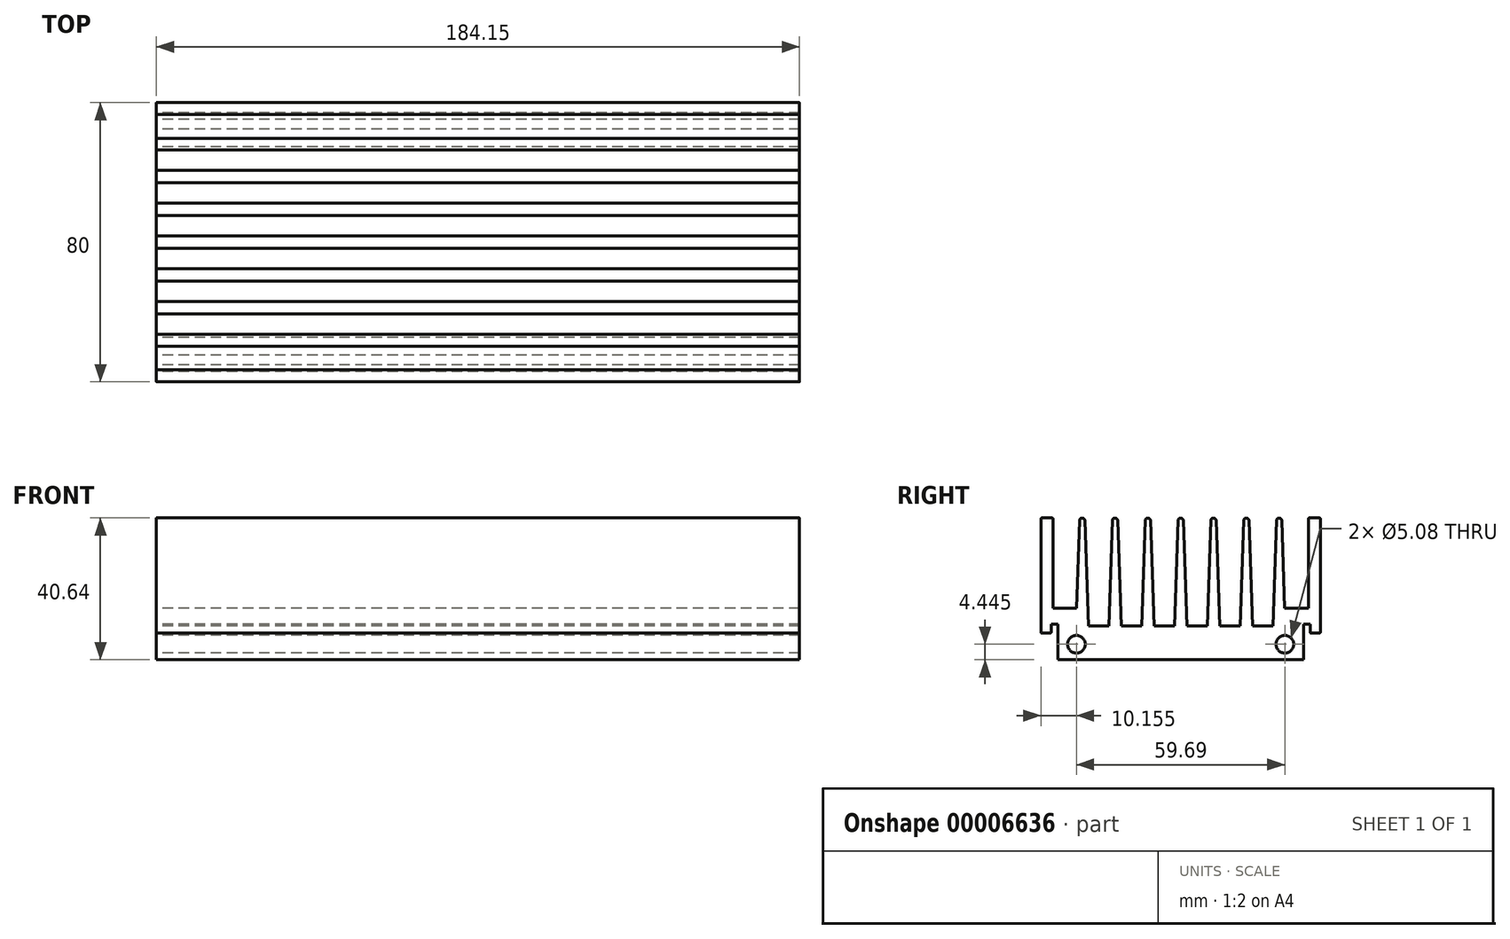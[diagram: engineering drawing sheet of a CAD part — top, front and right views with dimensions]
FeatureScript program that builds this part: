
annotation { "Feature Type Name" : "Feature", "Feature Type Description" : "" }
export const myFeature = defineFeature(function(context is Context, id is Id, definition is map)
    precondition{}
    {
        {
            var Q0;
            Q0=qCreatedBy(makeId("Right.planeOp"),FACE);
            var sketch = newSketch(context, id + "F0", { "sketchPlane" : qUnion([Q0])});
            skLineSegment(sketch, "E0", {"start": v(0, 0) * mm, "end": v(-35.18, 0) * mm});
            skLineSegment(sketch, "E1", {"start": v(-35.18, 0) * mm, "end": v(-35.18, 10.16) * mm});
            skLineSegment(sketch, "E2", {"start": v(-35.18, 10.16) * mm, "end": v(-37.08, 10.16) * mm});
            skLineSegment(sketch, "E3", {"start": v(-37.08, 10.16) * mm, "end": v(-37.08, 7.87) * mm});
            skLineSegment(sketch, "E4", {"start": v(-37.34, 7.62) * mm, "end": v(-39.75, 7.62) * mm});
            skLineSegment(sketch, "E5", {"start": v(-40, 7.87) * mm, "end": v(-40, 40.39) * mm});
            skLineSegment(sketch, "E6", {"start": v(-39.75, 40.64) * mm, "end": v(-36.83, 40.64) * mm});
            skLineSegment(sketch, "E7", {"start": v(-36.58, 40.39) * mm, "end": v(-36.58, 14.73) * mm});
            skLineSegment(sketch, "E8", {"start": v(-36.58, 14.73) * mm, "end": v(-29.8, 14.73) * mm});
            skLineSegment(sketch, "E9", {"start": v(0, -22.16) * mm, "end": v(0, 46.46) * mm, "construction": true});
            skLineSegment(sketch, "E10", {"start": v(-65.68, 9.65) * mm, "end": v(18.9, 9.65) * mm, "construction": true});
            skLineSegment(sketch, "E11", {"start": v(-69.07, 14.73) * mm, "end": v(15.35, 14.73) * mm, "construction": true});
            skLineSegment(sketch, "E12", {"start": v(-1.78, 43.71) * mm, "end": v(-1.78, -5.53) * mm, "construction": true});
            skLineSegment(sketch, "E13.0.MirrorCS", {"start": v(1.78, 43.71) * mm, "end": v(1.78, -5.53) * mm, "construction": true});
            skLineSegment(sketch, "E14", {"start": v(-1.78, 9.65) * mm, "end": v(-0.76, 39.88) * mm});
            skLineSegment(sketch, "E15", {"start": v(1.78, 9.65) * mm, "end": v(0.76, 39.88) * mm});
            skLineSegment(sketch, "E16", {"start": v(-71.84, 39.88) * mm, "end": v(8.54, 39.88) * mm, "construction": true});
            skArc(sketch, "E17", {"start": v(-0.76, 39.88) * mm, "mid": v(0, 40.61) * mm, "end": v(0.76, 39.88) * mm});
            skArc(sketch, "E18.1.0.0", {"start": v(-10.16, 39.88) * mm, "mid": v(-9.4, 40.61) * mm, "end": v(-8.64, 39.88) * mm});
            skLineSegment(sketch, "E18.1.0.1", {"start": v(-11.18, 9.65) * mm, "end": v(-10.16, 39.88) * mm});
            skLineSegment(sketch, "E18.1.0.2", {"start": v(-7.62, 9.65) * mm, "end": v(-8.64, 39.88) * mm});
            skLineSegment(sketch, "E18.1.0.3", {"start": v(-11.18, 9.65) * mm, "end": v(-17.02, 9.65) * mm});
            skArc(sketch, "E18.2.0.0", {"start": v(-19.56, 39.88) * mm, "mid": v(-18.8, 40.61) * mm, "end": v(-18.03, 39.88) * mm});
            skLineSegment(sketch, "E18.2.0.1", {"start": v(-20.57, 9.65) * mm, "end": v(-19.56, 39.88) * mm});
            skLineSegment(sketch, "E18.2.0.2", {"start": v(-17.02, 9.65) * mm, "end": v(-18.03, 39.88) * mm});
            skLineSegment(sketch, "E18.2.0.3", {"start": v(-20.57, 9.65) * mm, "end": v(-26.42, 9.65) * mm});
            skArc(sketch, "E18.3.0.0", {"start": v(-28.96, 39.88) * mm, "mid": v(-28.2, 40.61) * mm, "end": v(-27.43, 39.88) * mm});
            skLineSegment(sketch, "E18.3.0.1", {"start": v(-29.8, 14.73) * mm, "end": v(-28.96, 39.88) * mm});
            skLineSegment(sketch, "E18.3.0.2", {"start": v(-26.42, 9.65) * mm, "end": v(-27.43, 39.88) * mm});
            skLineSegment(sketch, "E18.direction1", {"start": v(-0.76, 39.88) * mm, "end": v(-10.16, 39.88) * mm, "construction": true});
            skPoint(sketch, "E19.end.orphan", {"position": v(-7.62, 9.65) * mm});
            skLineSegment(sketch, "E20", {"start": v(-7.62, 9.65) * mm, "end": v(-1.78, 9.65) * mm});
            skLineSegment(sketch, "E21.0.MirrorCS", {"start": v(0, 0) * mm, "end": v(35.18, 0) * mm});
            skLineSegment(sketch, "E21.1.MirrorCS", {"start": v(7.62, 9.65) * mm, "end": v(1.78, 9.65) * mm});
            skArc(sketch, "E21.2.MirrorCS", {"start": v(10.16, 39.88) * mm, "mid": v(9.4, 40.61) * mm, "end": v(8.64, 39.88) * mm});
            skArc(sketch, "E21.3.MirrorCS", {"start": v(28.96, 39.88) * mm, "mid": v(28.2, 40.61) * mm, "end": v(27.43, 39.88) * mm});
            skArc(sketch, "E21.4.MirrorCS", {"start": v(19.56, 39.88) * mm, "mid": v(18.8, 40.61) * mm, "end": v(18.03, 39.88) * mm});
            skLineSegment(sketch, "E21.5.MirrorCS", {"start": v(11.18, 9.65) * mm, "end": v(17.02, 9.65) * mm});
            skPoint(sketch, "E21.6.MirrorP", {"position": v(7.62, 9.65) * mm});
            skLineSegment(sketch, "E21.7.MirrorCS", {"start": v(11.18, 9.65) * mm, "end": v(10.16, 39.88) * mm});
            skLineSegment(sketch, "E21.8.MirrorCS", {"start": v(17.02, 9.65) * mm, "end": v(18.03, 39.88) * mm});
            skLineSegment(sketch, "E21.9.MirrorCS", {"start": v(26.42, 9.65) * mm, "end": v(27.43, 39.88) * mm});
            skLineSegment(sketch, "E21.10.MirrorCS", {"start": v(20.57, 9.65) * mm, "end": v(26.42, 9.65) * mm});
            skLineSegment(sketch, "E21.11.MirrorCS", {"start": v(37.34, 7.62) * mm, "end": v(39.75, 7.62) * mm});
            skLineSegment(sketch, "E21.12.MirrorCS", {"start": v(35.18, 0) * mm, "end": v(35.18, 10.16) * mm});
            skLineSegment(sketch, "E21.13.MirrorCS", {"start": v(7.62, 9.65) * mm, "end": v(8.64, 39.88) * mm});
            skLineSegment(sketch, "E21.14.MirrorCS", {"start": v(40, 7.87) * mm, "end": v(40, 40.39) * mm});
            skLineSegment(sketch, "E21.15.MirrorCS", {"start": v(35.18, 10.16) * mm, "end": v(37.08, 10.16) * mm});
            skLineSegment(sketch, "E21.16.MirrorCS", {"start": v(39.75, 40.64) * mm, "end": v(36.83, 40.64) * mm});
            skLineSegment(sketch, "E21.17.MirrorCS", {"start": v(36.58, 14.73) * mm, "end": v(29.8, 14.73) * mm});
            skLineSegment(sketch, "E21.18.MirrorCS", {"start": v(29.8, 14.73) * mm, "end": v(28.96, 39.88) * mm});
            skLineSegment(sketch, "E21.19.MirrorCS", {"start": v(37.08, 10.16) * mm, "end": v(37.08, 7.87) * mm});
            skLineSegment(sketch, "E21.20.MirrorCS", {"start": v(20.57, 9.65) * mm, "end": v(19.56, 39.88) * mm});
            skLineSegment(sketch, "E21.21.MirrorCS", {"start": v(36.58, 40.39) * mm, "end": v(36.58, 14.73) * mm});
            skPoint(sketch, "E22.visualSharp", {"position": v(-40, 40.64) * mm});
            skArc(sketch, "E22.filletArc", {"start": v(-39.75, 40.64) * mm, "mid": v(-39.93, 40.57) * mm, "end": v(-40, 40.39) * mm});
            skPoint(sketch, "E23.visualSharp", {"position": v(-36.58, 40.64) * mm});
            skArc(sketch, "E23.filletArc", {"start": v(-36.58, 40.39) * mm, "mid": v(-36.65, 40.57) * mm, "end": v(-36.83, 40.64) * mm});
            skPoint(sketch, "E24.visualSharp", {"position": v(-40, 7.62) * mm});
            skArc(sketch, "E24.filletArc", {"start": v(-40, 7.87) * mm, "mid": v(-39.93, 7.7) * mm, "end": v(-39.75, 7.62) * mm});
            skCircle(sketch, "E25", {"center": v(-29.85, 4.44) * mm, "radius": 2.54 * mm});
            skCircle(sketch, "E26.0.MirrorC", {"center": v(29.85, 4.44) * mm, "radius": 2.54 * mm});
            skPoint(sketch, "E27.visualSharp", {"position": v(36.58, 40.64) * mm});
            skArc(sketch, "E27.filletArc", {"start": v(36.83, 40.64) * mm, "mid": v(36.65, 40.57) * mm, "end": v(36.58, 40.39) * mm});
            skPoint(sketch, "E28.visualSharp", {"position": v(40, 40.64) * mm});
            skArc(sketch, "E28.filletArc", {"start": v(40, 40.39) * mm, "mid": v(39.93, 40.57) * mm, "end": v(39.75, 40.64) * mm});
            skPoint(sketch, "E29.visualSharp", {"position": v(-37.08, 7.62) * mm});
            skArc(sketch, "E29.filletArc", {"start": v(-37.34, 7.62) * mm, "mid": v(-37.16, 7.7) * mm, "end": v(-37.08, 7.87) * mm});
            skPoint(sketch, "E30.visualSharp", {"position": v(37.08, 7.62) * mm});
            skArc(sketch, "E30.filletArc", {"start": v(37.08, 7.87) * mm, "mid": v(37.16, 7.7) * mm, "end": v(37.34, 7.62) * mm});
            skPoint(sketch, "E31.visualSharp", {"position": v(40, 7.62) * mm});
            skArc(sketch, "E31.filletArc", {"start": v(39.75, 7.62) * mm, "mid": v(39.93, 7.7) * mm, "end": v(40, 7.87) * mm});
            skSolve(sketch);
        }
        {
            var Q0;
            Q0 = qSketchRegion(id + "F0", true);
            extrude(context, id + "F1", {"entities" : qUnion([Q0]), "depth" : 184.15 * mm});
        }
    });
